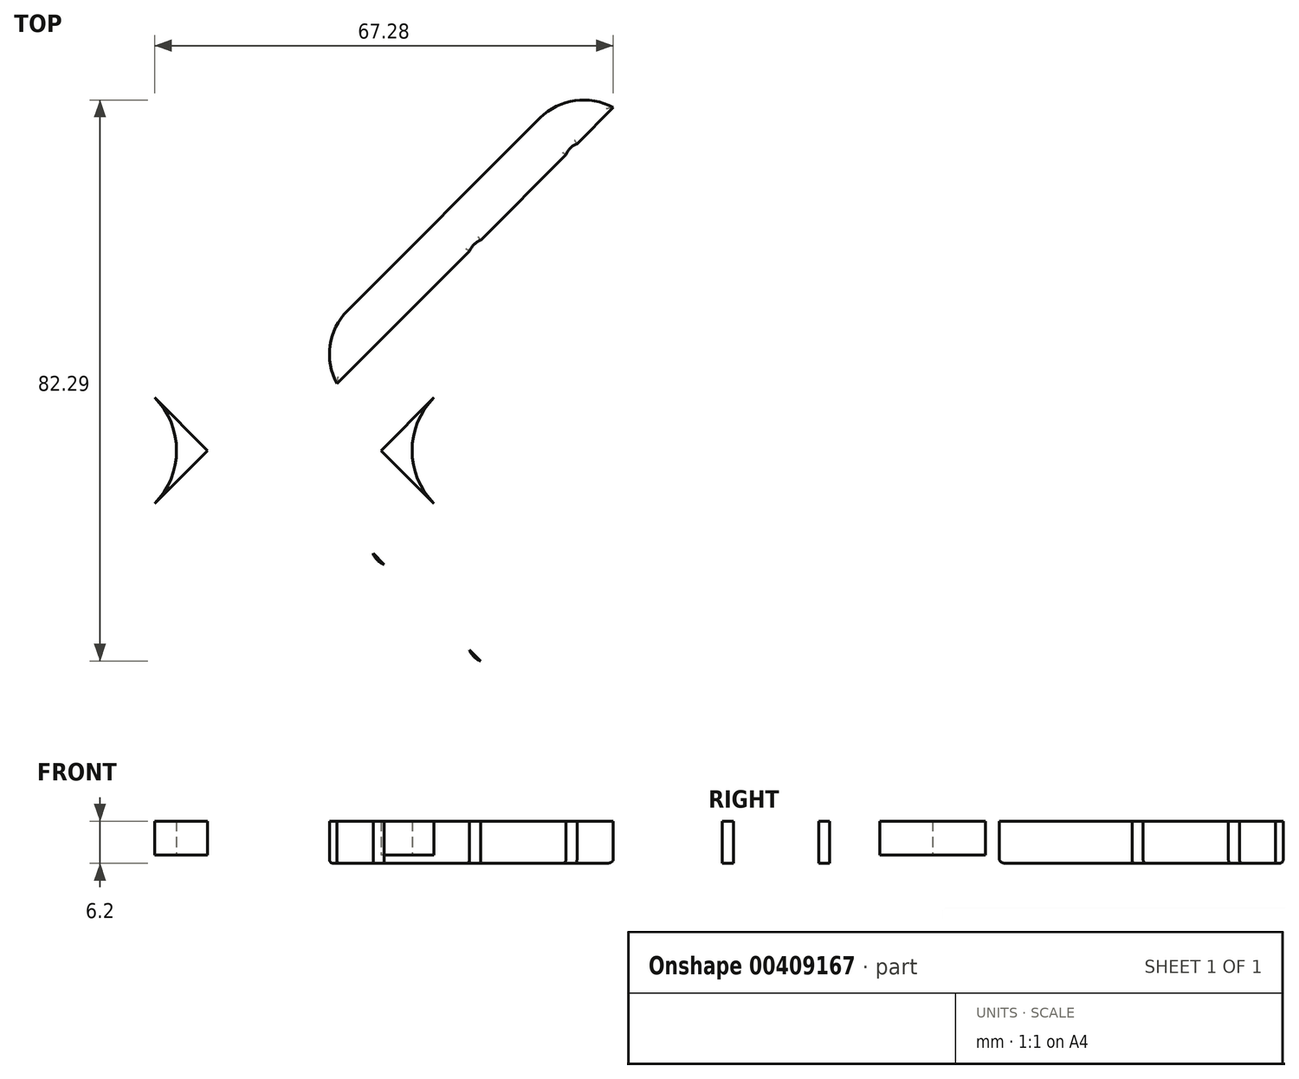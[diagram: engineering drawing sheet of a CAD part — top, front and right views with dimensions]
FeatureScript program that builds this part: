
annotation { "Feature Type Name" : "Feature", "Feature Type Description" : "" }
export const myFeature = defineFeature(function(context is Context, id is Id, definition is map)
    precondition{}
    {
        {
            var Q0;
            Q0=qCreatedBy(makeId("Top.planeOp"),FACE);
            var sketch = newSketch(context, id + "F0", { "sketchPlane" : qUnion([Q0])});
            skLineSegment(sketch, "E0", {"start": v(0, 0) * mm, "end": v(56.79, 56.79) * mm, "construction": true});
            skLineSegment(sketch, "E1", {"start": v(56.79, -56.79) * mm, "end": v(0, 0) * mm, "construction": true});
            skLineSegment(sketch, "E2", {"start": v(0, 14.14) * mm, "end": v(14.14, 0) * mm, "construction": true});
            skCircle(sketch, "E3", {"center": v(14.14, 14.14) * mm, "radius": 10 * mm, "construction": true});
            skCircle(sketch, "E4", {"center": v(14.14, 14.14) * mm, "radius": 2.75 * mm, "construction": true});
            skCircle(sketch, "E5", {"center": v(28.28, 28.28) * mm, "radius": 2.75 * mm});
            skCircle(sketch, "E6", {"center": v(42.43, 42.43) * mm, "radius": 2.75 * mm});
            skArc(sketch, "E7", {"start": v(7.78, 20.5) * mm, "mid": v(5.28, 12.58) * mm, "end": v(10.33, 5.99) * mm});
            skArc(sketch, "E8", {"start": v(48.8, 36.06) * mm, "mid": v(48.8, 48.8) * mm, "end": v(36.06, 48.8) * mm});
            skLineSegment(sketch, "E9", {"start": v(7.78, 20.5) * mm, "end": v(36.06, 48.8) * mm});
            skCircle(sketch, "E10.MirrorC", {"center": v(14.14, -14.14) * mm, "radius": 2.75 * mm});
            skLineSegment(sketch, "E11.MirrorCS", {"start": v(0, -14.14) * mm, "end": v(14.14, 0) * mm, "construction": true});
            skCircle(sketch, "E12.MirrorC", {"center": v(28.28, -28.28) * mm, "radius": 2.75 * mm});
            skArc(sketch, "E13.MirrorCS", {"start": v(7.78, -20.5) * mm, "mid": v(5.28, -12.58) * mm, "end": v(10.33, -5.99) * mm});
            skCircle(sketch, "E14.MirrorC", {"center": v(14.14, -14.14) * mm, "radius": 10 * mm, "construction": true});
            skLineSegment(sketch, "E15.MirrorCS", {"start": v(7.78, -20.5) * mm, "end": v(21.92, -34.65) * mm});
            skArc(sketch, "E16", {"start": v(10.33, 5.99) * mm, "mid": v(14.14, 0) * mm, "end": v(10.33, -5.99) * mm, "construction": true});
            skCircle(sketch, "E17", {"center": v(28.28, 28.28) * mm, "radius": 2.5 * mm, "construction": true});
            skLineSegment(sketch, "E18", {"start": v(50.3, 46.77) * mm, "end": v(9.8, 6.26) * mm});
            skLineSegment(sketch, "E19.MirrorCS", {"start": v(46.77, 50.3) * mm, "end": v(6.26, 9.8) * mm});
            skLineSegment(sketch, "E20.MirrorCS", {"start": v(32.63, -36.17) * mm, "end": v(6.26, -9.8) * mm});
            skLineSegment(sketch, "E21.MirrorCS", {"start": v(36.17, -32.63) * mm, "end": v(9.8, -6.26) * mm});
            skArc(sketch, "E22", {"start": v(7.78, 20.5) * mm, "mid": v(-0.72, 0) * mm, "end": v(7.78, -20.5) * mm});
            skCircle(sketch, "E23", {"center": v(0, 0) * mm, "radius": 2.75 * mm, "construction": true});
            skLineSegment(sketch, "E24", {"start": v(14.14, 0) * mm, "end": v(-0.72, 0) * mm, "construction": true});
            skLineSegment(sketch, "E25", {"start": v(13.86, 0) * mm, "end": v(1.88, -11.98) * mm, "construction": true});
            skLineSegment(sketch, "E26.MirrorCS", {"start": v(13.86, 0) * mm, "end": v(1.88, 11.98) * mm, "construction": true});
            skLineSegment(sketch, "E27", {"start": v(48.8, 36.06) * mm, "end": v(12.73, 0) * mm});
            skLineSegment(sketch, "E28.MirrorCS", {"start": v(34.65, -21.92) * mm, "end": v(12.73, 0) * mm});
            skArc(sketch, "E29", {"start": v(20.5, 7.78) * mm, "mid": v(17.28, 0) * mm, "end": v(20.5, -7.78) * mm});
            skArc(sketch, "E30", {"start": v(21.92, -34.65) * mm, "mid": v(34.65, -34.65) * mm, "end": v(34.65, -21.92) * mm});
            skSolve(sketch);
        }
        {
            var Q0;
            {var subQ4=sQuery(id+"F0.wireOp",EDGE,"E16");Q0=makeQuery(id+"F0.imprint","IMPRINT",FACE,{"disambiguationData":[TD([[makeQuery(id+"F0.imprint","IMPRINT",EDGE,{"derivedFrom":subQ4}),1.0]])]});}
            var Q1;
            {var subQ0=sQuery(id+"F0.wireOp",EDGE,"E9");Q1=makeQuery(id+"F0.imprint","IMPRINT",FACE,{"disambiguationData":[TD([[makeQuery(id+"F0.imprint","IMPRINT",EDGE,{"derivedFrom":subQ0}),-1.0]])]});}
            var Q2;
            {var subQ0=sQuery(id+"F0.wireOp",EDGE,"E19.MirrorCS");var subQ1=sQuery(id+"F0.wireOp",EDGE,"E5");var subQ2=makeQuery(id+"F0.imprint","INTERSECT",VERTEX,{"disambiguationData":[OD(1.0)],"derivedFrom":[subQ1,subQ0]});Q2=makeQuery(id+"F0.imprint","IMPRINT",FACE,{"disambiguationData":[TD([[makeQuery(id+"F0.imprint","IMPRINT",EDGE,{"disambiguationData":[TD([[subQ2,1.0]])],"derivedFrom":subQ1}),-1.0]])]});}
            var Q3;
            {var subQ0=sQuery(id+"F0.wireOp",EDGE,"E19.MirrorCS");var subQ1=sQuery(id+"F0.wireOp",EDGE,"E6");var subQ2=makeQuery(id+"F0.imprint","INTERSECT",VERTEX,{"disambiguationData":[OD(1.0)],"derivedFrom":[subQ1,subQ0]});Q3=makeQuery(id+"F0.imprint","IMPRINT",FACE,{"disambiguationData":[TD([[makeQuery(id+"F0.imprint","IMPRINT",EDGE,{"disambiguationData":[TD([[subQ2,1.0]])],"derivedFrom":subQ1}),-1.0]])]});}
            var Q4;
            {var subQ0=sQuery(id+"F0.wireOp",EDGE,"E19.MirrorCS");var subQ1=sQuery(id+"F0.wireOp",EDGE,"E4");var subQ2=makeQuery(id+"F0.imprint","INTERSECT",VERTEX,{"disambiguationData":[OD(1.0)],"derivedFrom":[subQ1,subQ0]});Q4=makeQuery(id+"F0.imprint","IMPRINT",FACE,{"disambiguationData":[TD([[makeQuery(id+"F0.imprint","IMPRINT",EDGE,{"disambiguationData":[TD([[subQ2,1.0]])],"derivedFrom":subQ1}),-1.0]])]});}
            var Q5;
            {var subQ0=sQuery(id+"F0.wireOp",EDGE,"E19.MirrorCS");var subQ1=sQuery(id+"F0.wireOp",EDGE,"E4");var subQ2=makeQuery(id+"F0.imprint","INTERSECT",VERTEX,{"disambiguationData":[OD(0.0)],"derivedFrom":[subQ1,subQ0]});Q5=makeQuery(id+"F0.imprint","IMPRINT",FACE,{"disambiguationData":[TD([[makeQuery(id+"F0.imprint","IMPRINT",EDGE,{"disambiguationData":[TD([[subQ2,-1.0]])],"derivedFrom":subQ1}),-1.0]])]});}
            var Q6;
            {var subQ0=sQuery(id+"F0.wireOp",EDGE,"E20.MirrorCS");var subQ1=sQuery(id+"F0.wireOp",EDGE,"E10.MirrorC");var subQ2=makeQuery(id+"F0.imprint","INTERSECT",VERTEX,{"disambiguationData":[OD(0.0)],"derivedFrom":[subQ1,subQ0]});Q6=makeQuery(id+"F0.imprint","IMPRINT",FACE,{"disambiguationData":[TD([[makeQuery(id+"F0.imprint","IMPRINT",EDGE,{"disambiguationData":[TD([[subQ2,-1.0]])],"derivedFrom":subQ1}),1.0]])]});}
            var Q7;
            {var subQ0=sQuery(id+"F0.wireOp",EDGE,"E20.MirrorCS");var subQ1=sQuery(id+"F0.wireOp",EDGE,"E10.MirrorC");var subQ2=makeQuery(id+"F0.imprint","INTERSECT",VERTEX,{"disambiguationData":[OD(1.0)],"derivedFrom":[subQ1,subQ0]});Q7=makeQuery(id+"F0.imprint","IMPRINT",FACE,{"disambiguationData":[TD([[makeQuery(id+"F0.imprint","IMPRINT",EDGE,{"disambiguationData":[TD([[subQ2,1.0]])],"derivedFrom":subQ1}),1.0]])]});}
            var Q8;
            {var subQ0=sQuery(id+"F0.wireOp",EDGE,"E20.MirrorCS");var subQ1=sQuery(id+"F0.wireOp",EDGE,"E12.MirrorC");var subQ2=makeQuery(id+"F0.imprint","INTERSECT",VERTEX,{"disambiguationData":[OD(1.0)],"derivedFrom":[subQ1,subQ0]});Q8=makeQuery(id+"F0.imprint","IMPRINT",FACE,{"disambiguationData":[TD([[makeQuery(id+"F0.imprint","IMPRINT",EDGE,{"disambiguationData":[TD([[subQ2,1.0]])],"derivedFrom":subQ1}),1.0]])]});}
            var Q9;
            {var subQ0=sQuery(id+"F0.wireOp",EDGE,"E20.MirrorCS");var subQ1=sQuery(id+"F0.wireOp",EDGE,"d5c651c2-006d-457a-9835-fe27e9ba46113.MirrorC");var subQ2=makeQuery(id+"F0.imprint","INTERSECT",VERTEX,{"disambiguationData":[OD(1.0)],"derivedFrom":[subQ1,subQ0]});Q9=makeQuery(id+"F0.imprint","IMPRINT",FACE,{"disambiguationData":[TD([[makeQuery(id+"F0.imprint","IMPRINT",EDGE,{"disambiguationData":[TD([[subQ2,1.0]])],"derivedFrom":subQ1}),1.0]])]});}
            var Q10;
            {var subQ0=sQuery(id+"F0.wireOp",EDGE,"E15.MirrorCS");Q10=makeQuery(id+"F0.imprint","IMPRINT",FACE,{"disambiguationData":[TD([[makeQuery(id+"F0.imprint","IMPRINT",EDGE,{"derivedFrom":subQ0}),1.0]])]});}
            var Q11;
            {var subQ3=sQuery(id+"F0.wireOp",EDGE,"E16");Q11=makeQuery(id+"F0.imprint","IMPRINT",FACE,{"disambiguationData":[TD([[makeQuery(id+"F0.imprint","IMPRINT",EDGE,{"derivedFrom":subQ3}),-1.0]])]});}
            var Q12;
            {var subQ1=sQuery(id+"F0.wireOp",EDGE,"E2");var subQ3=sQuery(id+"F0.wireOp",EDGE,"E22");var subQ4=makeQuery(id+"F0.imprint","INTERSECT",VERTEX,{"derivedFrom":[subQ1,subQ3]});Q12=makeQuery(id+"F0.imprint","IMPRINT",FACE,{"disambiguationData":[TD([[makeQuery(id+"F0.imprint","IMPRINT",EDGE,{"disambiguationData":[TD([[subQ4,-1.0]])],"derivedFrom":subQ3}),1.0]])]});}
            var Q13;
            {var subQ3=sQuery(id+"F0.wireOp",EDGE,"E29");Q13=makeQuery(id+"F0.imprint","IMPRINT",FACE,{"disambiguationData":[TD([[makeQuery(id+"F0.imprint","IMPRINT",EDGE,{"derivedFrom":subQ3}),-1.0]])]});}
            var Q14;
            {var subQ0=sQuery(id+"F0.wireOp",EDGE,"E19.MirrorCS");var subQ1=sQuery(id+"F0.wireOp",EDGE,"E6");var subQ2=makeQuery(id+"F0.imprint","INTERSECT",VERTEX,{"disambiguationData":[OD(0.0)],"derivedFrom":[subQ1,subQ0]});Q14=makeQuery(id+"F0.imprint","IMPRINT",FACE,{"disambiguationData":[TD([[makeQuery(id+"F0.imprint","IMPRINT",EDGE,{"disambiguationData":[TD([[subQ2,-1.0]])],"derivedFrom":subQ1}),-1.0]])]});}
            var Q15;
            {var subQ0=sQuery(id+"F0.wireOp",EDGE,"E19.MirrorCS");var subQ1=sQuery(id+"F0.wireOp",EDGE,"E5");var subQ2=makeQuery(id+"F0.imprint","INTERSECT",VERTEX,{"disambiguationData":[OD(0.0)],"derivedFrom":[subQ1,subQ0]});Q15=makeQuery(id+"F0.imprint","IMPRINT",FACE,{"disambiguationData":[TD([[makeQuery(id+"F0.imprint","IMPRINT",EDGE,{"disambiguationData":[TD([[subQ2,-1.0]])],"derivedFrom":subQ1}),-1.0]])]});}
            extrude(context, id + "F1", {"entities" : qUnion([Q0, Q1, Q2, Q3, Q4, Q5, Q6, Q7, Q8, Q9, Q10, Q11, Q12, Q13, Q14, Q15]), "depth" : 5 * mm, "offsetDistance" : 25 * mm});
        }
        {
            var Q0;
            {var subQ0=sQuery(id+"F0.wireOp",EDGE,"E20.MirrorCS");var subQ1=sQuery(id+"F0.wireOp",EDGE,"E12.MirrorC");var subQ2=makeQuery(id+"F0.imprint","INTERSECT",VERTEX,{"disambiguationData":[OD(1.0)],"derivedFrom":[subQ1,subQ0]});Q0=makeQuery(id+"F0.imprint","IMPRINT",FACE,{"disambiguationData":[TD([[makeQuery(id+"F0.imprint","IMPRINT",EDGE,{"disambiguationData":[TD([[subQ2,1.0]])],"derivedFrom":subQ1}),1.0]])]});}
            var Q1;
            {var subQ0=sQuery(id+"F0.wireOp",EDGE,"E20.MirrorCS");var subQ1=sQuery(id+"F0.wireOp",EDGE,"E10.MirrorC");var subQ2=makeQuery(id+"F0.imprint","INTERSECT",VERTEX,{"disambiguationData":[OD(1.0)],"derivedFrom":[subQ1,subQ0]});Q1=makeQuery(id+"F0.imprint","IMPRINT",FACE,{"disambiguationData":[TD([[makeQuery(id+"F0.imprint","IMPRINT",EDGE,{"disambiguationData":[TD([[subQ2,1.0]])],"derivedFrom":subQ1}),1.0]])]});}
            var Q2;
            {var subQ0=sQuery(id+"F0.wireOp",EDGE,"E19.MirrorCS");var subQ1=sQuery(id+"F0.wireOp",EDGE,"E4");var subQ2=makeQuery(id+"F0.imprint","INTERSECT",VERTEX,{"disambiguationData":[OD(1.0)],"derivedFrom":[subQ1,subQ0]});Q2=makeQuery(id+"F0.imprint","IMPRINT",FACE,{"disambiguationData":[TD([[makeQuery(id+"F0.imprint","IMPRINT",EDGE,{"disambiguationData":[TD([[subQ2,1.0]])],"derivedFrom":subQ1}),-1.0]])]});}
            var Q3;
            {var subQ0=sQuery(id+"F0.wireOp",EDGE,"E19.MirrorCS");var subQ1=sQuery(id+"F0.wireOp",EDGE,"E5");var subQ2=makeQuery(id+"F0.imprint","INTERSECT",VERTEX,{"disambiguationData":[OD(1.0)],"derivedFrom":[subQ1,subQ0]});Q3=makeQuery(id+"F0.imprint","IMPRINT",FACE,{"disambiguationData":[TD([[makeQuery(id+"F0.imprint","IMPRINT",EDGE,{"disambiguationData":[TD([[subQ2,1.0]])],"derivedFrom":subQ1}),-1.0]])]});}
            var Q4;
            {var subQ0=sQuery(id+"F0.wireOp",EDGE,"E19.MirrorCS");var subQ1=sQuery(id+"F0.wireOp",EDGE,"E6");var subQ2=makeQuery(id+"F0.imprint","INTERSECT",VERTEX,{"disambiguationData":[OD(1.0)],"derivedFrom":[subQ1,subQ0]});Q4=makeQuery(id+"F0.imprint","IMPRINT",FACE,{"disambiguationData":[TD([[makeQuery(id+"F0.imprint","IMPRINT",EDGE,{"disambiguationData":[TD([[subQ2,1.0]])],"derivedFrom":subQ1}),-1.0]])]});}
            extrude(context, id + "F2", {"entities" : qUnion([Q0, Q1, Q2, Q3, Q4]), "operationType" : NewBodyOperationType.ADD, "oppositeDirection" : true, "depth" : 1.2 * mm, "offsetDistance" : 25 * mm});
        }
        {
            var Q0;
            Q0=makeQuery(id+"F2.opExtrude","CAP_FACE",FACE,{"disambiguationData":[OSD([sQuery(id+"F0.wireOp",EDGE,"E5"),sQuery(id+"F0.wireOp",EDGE,"E6"),sQuery(id+"F0.wireOp",EDGE,"E18"),sQuery(id+"F0.wireOp",EDGE,"E19.MirrorCS")])],"isStart":false});
            var Q1;
            Q1=makeQuery(id+"F2.opExtrude","CAP_FACE",FACE,{"disambiguationData":[OSD([sQuery(id+"F0.wireOp",EDGE,"E6"),sQuery(id+"F0.wireOp",EDGE,"E8"),sQuery(id+"F0.wireOp",EDGE,"E18"),sQuery(id+"F0.wireOp",EDGE,"E19.MirrorCS")])],"isStart":false});
            var Q2;
            Q2=makeQuery(id+"F2.opExtrude","CAP_FACE",FACE,{"disambiguationData":[OSD([sQuery(id+"F0.wireOp",EDGE,"E4"),sQuery(id+"F0.wireOp",EDGE,"E5"),sQuery(id+"F0.wireOp",EDGE,"E18"),sQuery(id+"F0.wireOp",EDGE,"E19.MirrorCS")])],"isStart":false});
            var Q3;
            Q3=makeQuery(id+"F2.opExtrude","CAP_FACE",FACE,{"disambiguationData":[OSD([sQuery(id+"F0.wireOp",EDGE,"E4"),sQuery(id+"F0.wireOp",EDGE,"E7"),sQuery(id+"F0.wireOp",EDGE,"E18"),sQuery(id+"F0.wireOp",EDGE,"E19.MirrorCS")])],"isStart":false});
            var Q4;
            Q4=makeQuery(id+"F2.opExtrude","CAP_FACE",FACE,{"disambiguationData":[OSD([sQuery(id+"F0.wireOp",EDGE,"E10.MirrorC"),sQuery(id+"F0.wireOp",EDGE,"E13.MirrorCS"),sQuery(id+"F0.wireOp",EDGE,"E20.MirrorCS"),sQuery(id+"F0.wireOp",EDGE,"E21.MirrorCS")])],"isStart":false});
            var Q5;
            Q5=makeQuery(id+"F2.opExtrude","CAP_FACE",FACE,{"disambiguationData":[OSD([sQuery(id+"F0.wireOp",EDGE,"E10.MirrorC"),sQuery(id+"F0.wireOp",EDGE,"E12.MirrorC"),sQuery(id+"F0.wireOp",EDGE,"E20.MirrorCS"),sQuery(id+"F0.wireOp",EDGE,"E21.MirrorCS")])],"isStart":false});
            var Q6;
            Q6=makeQuery(id+"F2.opExtrude","CAP_FACE",FACE,{"disambiguationData":[OSD([sQuery(id+"F0.wireOp",EDGE,"d5c651c2-006d-457a-9835-fe27e9ba46113.MirrorC"),sQuery(id+"F0.wireOp",EDGE,"d5c651c2-006d-457a-9835-fe27e9ba46117.MirrorCS"),sQuery(id+"F0.wireOp",EDGE,"E20.MirrorCS"),sQuery(id+"F0.wireOp",EDGE,"E21.MirrorCS")])],"isStart":false});
            var Q7;
            Q7=makeQuery(id+"F2.opExtrude","CAP_FACE",FACE,{"disambiguationData":[OSD([sQuery(id+"F0.wireOp",EDGE,"E12.MirrorC"),sQuery(id+"F0.wireOp",EDGE,"d5c651c2-006d-457a-9835-fe27e9ba46113.MirrorC"),sQuery(id+"F0.wireOp",EDGE,"E20.MirrorCS"),sQuery(id+"F0.wireOp",EDGE,"E21.MirrorCS")])],"isStart":false});
            var Q8;
            Q8=makeQuery(id+"F2.opExtrude","CAP_FACE",FACE,{"disambiguationData":[OSD([sQuery(id+"F0.wireOp",EDGE,"E2"),sQuery(id+"F0.wireOp",EDGE,"AwdjGCNM-xevV-rkCu-k57T-VdCHvtGFgJDu"),sQuery(id+"F0.wireOp",EDGE,"E22")])],"isStart":false});
            fillet(context, id + "F3", {"entities" : qUnion([Q0, Q1, Q2, Q3, Q4, Q5, Q6, Q7, Q8]), "radius" : 0.6 * mm, "tangentPropagation" : true, "allowEdgeOverflow" : false});
        }
        {
            var Q0;
            Q0=makeQuery(id+"F1.opExtrude","SWEPT_BODY",BODY,{"disambiguationData":[OSD([sQuery(id+"F0.wireOp",EDGE,"E5"),sQuery(id+"F0.wireOp",EDGE,"E6"),sQuery(id+"F0.wireOp",EDGE,"E8"),sQuery(id+"F0.wireOp",EDGE,"E9"),sQuery(id+"F0.wireOp",EDGE,"E10.MirrorC"),sQuery(id+"F0.wireOp",EDGE,"E12.MirrorC"),sQuery(id+"F0.wireOp",EDGE,"E15.MirrorCS"),sQuery(id+"F0.wireOp",EDGE,"E22"),sQuery(id+"F0.wireOp",EDGE,"E27"),sQuery(id+"F0.wireOp",EDGE,"E28.MirrorCS"),sQuery(id+"F0.wireOp",EDGE,"E29"),sQuery(id+"F0.wireOp",EDGE,"E30")])]});
            var Q1;
            Q1=qCreatedBy(makeId("Right.planeOp"),FACE);
            mirror(context, id + "F4", {"entities" : qUnion([Q0]), "mirrorPlane" : qUnion([Q1])});
        }
    });
